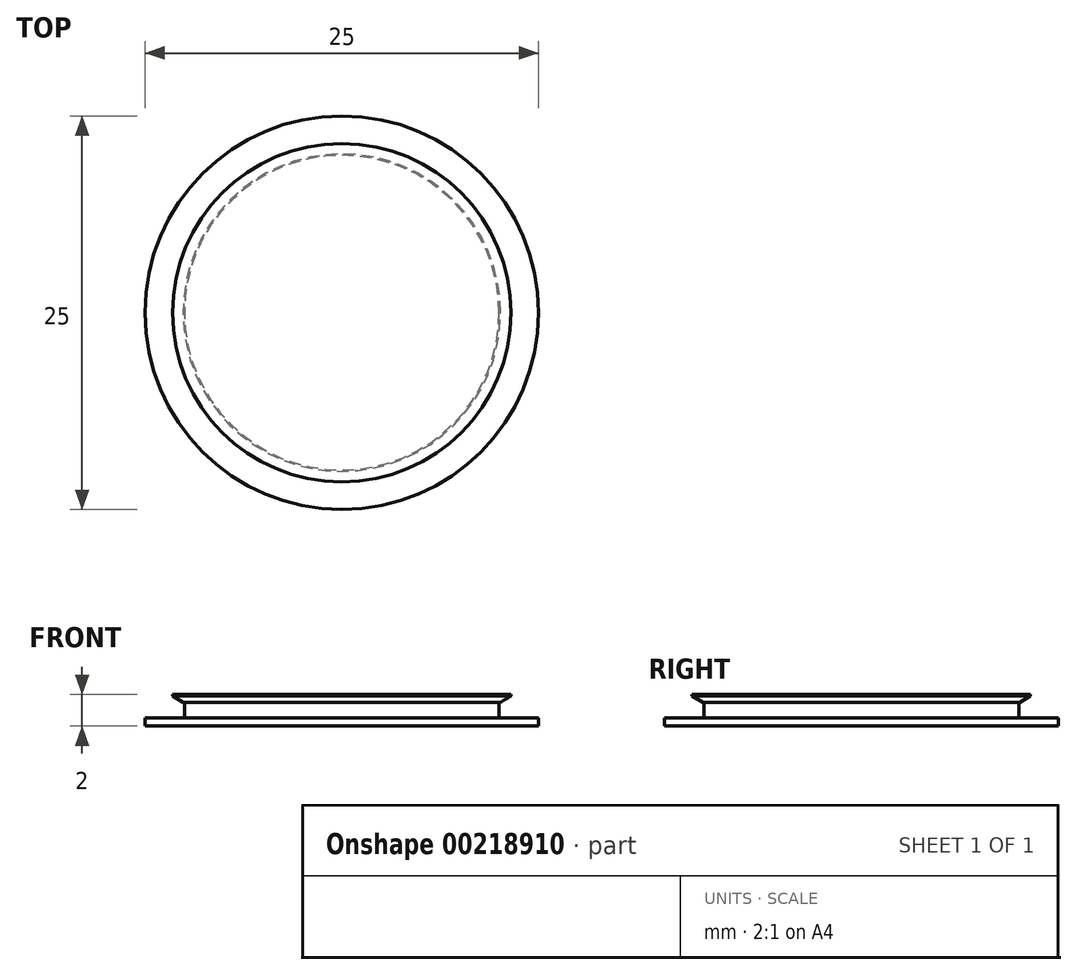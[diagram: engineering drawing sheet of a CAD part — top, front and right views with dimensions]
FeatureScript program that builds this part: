
annotation { "Feature Type Name" : "Feature", "Feature Type Description" : "" }
export const myFeature = defineFeature(function(context is Context, id is Id, definition is map)
    precondition{}
    {
        {
            var Q0;
            Q0=qCreatedBy(makeId("Top.planeOp"),FACE);
            var sketch = newSketch(context, id + "F0", { "sketchPlane" : qUnion([Q0])});
            skCircle(sketch, "E0", {"center": v(0, 0) * mm, "radius": 12.5 * mm});
            skSolve(sketch);
        }
        {
            var Q0;
            Q0=makeQuery(id+"F0.imprint","IMPRINT",FACE,{"disambiguationData":[TD([[makeQuery(id+"F0.imprint","IMPRINT",EDGE,{"derivedFrom":sQuery(id+"F0.wireOp",EDGE,"E0")}),1.0]])]});
            extrude(context, id + "F1", {"entities" : qUnion([Q0]), "depth" : 0.5 * mm});
        }
        {
            var Q0;
            Q0=makeQuery(id+"F1.opExtrude","CAP_FACE",FACE,{"disambiguationData":[OSD([sQuery(id+"F0.wireOp",EDGE,"E0")])],"isStart":false});
            var sketch = newSketch(context, id + "F2", { "sketchPlane" : qUnion([Q0])});
            skCircle(sketch, "E1", {"center": v(0, 0) * mm, "radius": 10 * mm});
            skSolve(sketch);
        }
        {
            var Q0;
            Q0=makeQuery(id+"F2.imprint","IMPRINT",FACE,{"disambiguationData":[TD([[makeQuery(id+"F2.imprint","IMPRINT",EDGE,{"derivedFrom":sQuery(id+"F2.wireOp",EDGE,"E1")}),1.0]])]});
            extrude(context, id + "F3", {"entities" : qUnion([Q0]), "operationType" : NewBodyOperationType.ADD, "depth" : 1 * mm});
        }
        {
            var Q0;
            Q0=makeQuery(id+"F3.opExtrude","CAP_FACE",FACE,{"disambiguationData":[OSD([sQuery(id+"F2.wireOp",EDGE,"E1")])],"isStart":false});
            var sketch = newSketch(context, id + "F4", { "sketchPlane" : qUnion([Q0])});
            skCircle(sketch, "E2", {"center": v(0, 0) * mm, "radius": 10.75 * mm});
            skSolve(sketch);
        }
        {
            var Q0;
            Q0=makeQuery(id+"F4.imprint","IMPRINT",FACE,{"disambiguationData":[TD([[makeQuery(id+"F4.imprint","IMPRINT",EDGE,{"derivedFrom":makeQuery(id+"F3.opExtrude","CAP_EDGE",EDGE,{"disambiguationData":[OSD([sQuery(id+"F2.wireOp",EDGE,"E1")])],"isStart":false})}),1.0]])]});
            var Q1;
            Q1=makeQuery(id+"F4.imprint","IMPRINT",FACE,{"disambiguationData":[TD([[makeQuery(id+"F4.imprint","IMPRINT",EDGE,{"derivedFrom":sQuery(id+"F4.wireOp",EDGE,"E2")}),1.0]])]});
            extrude(context, id + "F5", {"entities" : qUnion([Q0, Q1]), "operationType" : NewBodyOperationType.ADD, "depth" : 0.5 * mm});
        }
        {
            var Q0;
            Q0=qCreatedBy(makeId("Front.planeOp"),FACE);
            var sketch = newSketch(context, id + "F6", { "sketchPlane" : qUnion([Q0])});
            skLineSegment(sketch, "E3", {"start": v(-10.03, 1.47) * mm, "end": v(-10.82, 1.95) * mm});
            skLineSegment(sketch, "E4", {"start": v(-10.82, 1.95) * mm, "end": v(-10.82, 1.45) * mm});
            skLineSegment(sketch, "E5", {"start": v(-10.82, 1.45) * mm, "end": v(-10.03, 1.47) * mm});
            skLineSegment(sketch, "E6", {"start": v(0, 0) * mm, "end": v(0, 4.07) * mm, "construction": true});
            skSolve(sketch);
        }
        {
            var Q0;
            Q0=makeQuery(id+"F6.imprint","IMPRINT",FACE,{"disambiguationData":[TD([[makeQuery(id+"F6.imprint","IMPRINT",EDGE,{"derivedFrom":sQuery(id+"F6.wireOp",EDGE,"E3")}),1.0]])]});
            var Q1;
            Q1=sQuery(id+"F6.wireOp",EDGE,"E6");
            revolve(context, id + "F7", {"operationType" : NewBodyOperationType.REMOVE, "entities" : qUnion([Q0]), "axis" : qUnion([Q1]), "revolveType" : RevolveType.FULL, "oppositeDirection" : true});
        }
    });
